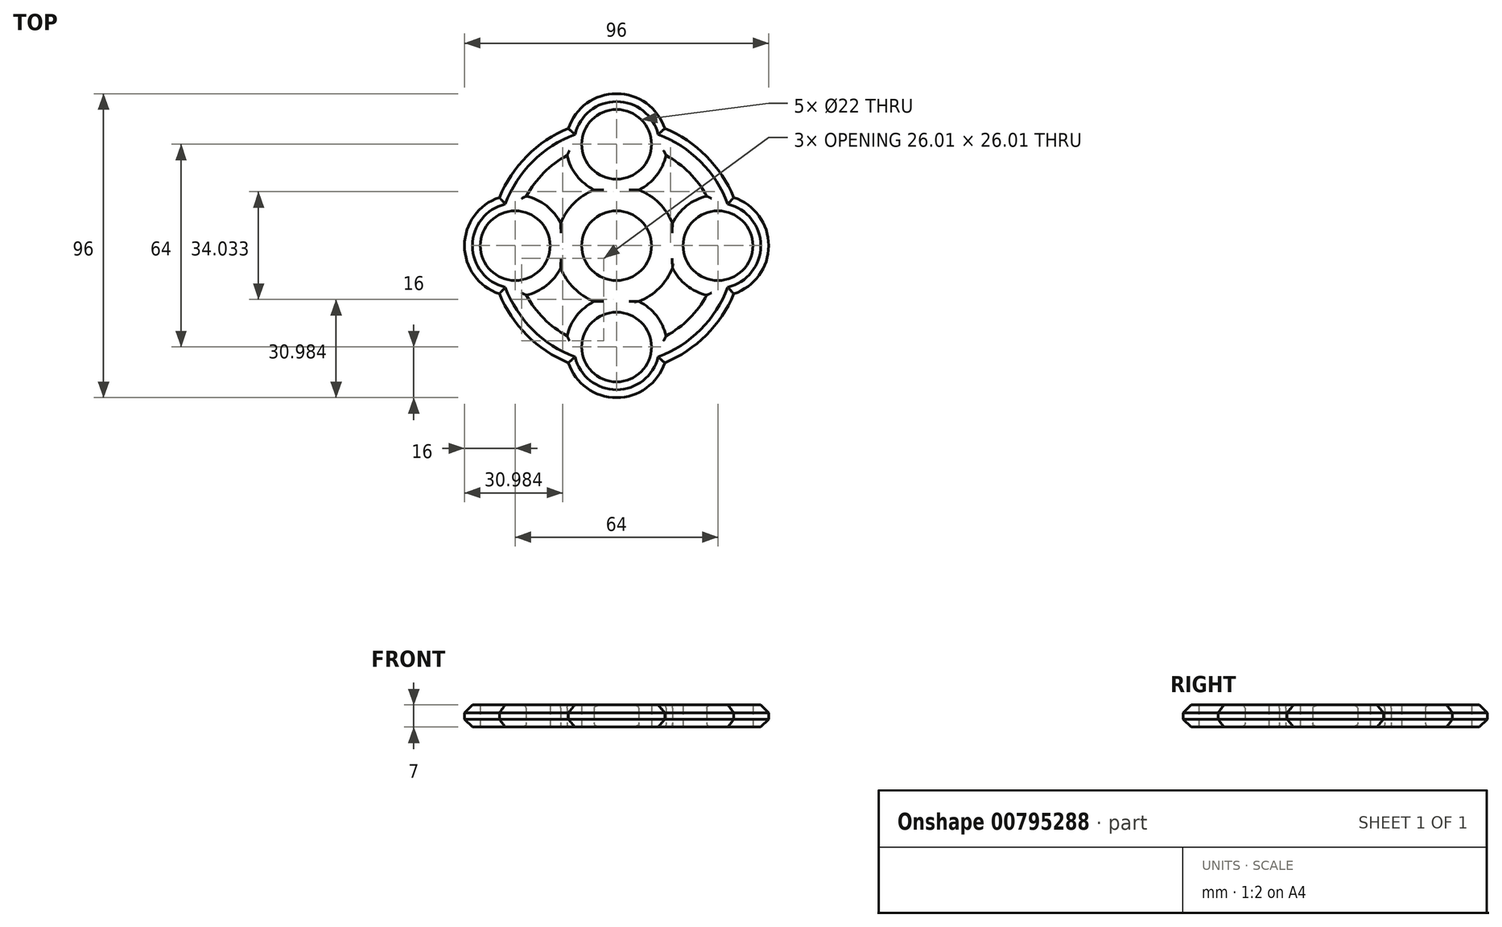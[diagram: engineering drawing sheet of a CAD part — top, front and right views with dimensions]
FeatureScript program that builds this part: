
annotation { "Feature Type Name" : "Feature", "Feature Type Description" : "" }
export const myFeature = defineFeature(function(context is Context, id is Id, definition is map)
    precondition{}
    {
        {
            var Q0;
            Q0=qCreatedBy(makeId("Top.planeOp"),FACE);
            var sketch = newSketch(context, id + "F0", { "sketchPlane" : qUnion([Q0])});
            skCircle(sketch, "E0", {"center": v(0, 0) * mm, "radius": 11 * mm});
            skCircle(sketch, "E1", {"center": v(0, 0) * mm, "radius": 19 * mm});
            skCircle(sketch, "E2", {"center": v(0, 0) * mm, "radius": 40 * mm});
            skCircle(sketch, "E3", {"center": v(0, 0) * mm, "radius": 32.5 * mm});
            skCircle(sketch, "E4", {"center": v(0, 32) * mm, "radius": 11 * mm});
            skCircle(sketch, "E5", {"center": v(0, 32) * mm, "radius": 16 * mm});
            skCircle(sketch, "E6.1.0", {"center": v(-32, 0) * mm, "radius": 16 * mm});
            skCircle(sketch, "E6.1.1", {"center": v(-32, 0) * mm, "radius": 11 * mm});
            skCircle(sketch, "E6.2.0", {"center": v(0, -32) * mm, "radius": 16 * mm});
            skCircle(sketch, "E6.2.1", {"center": v(0, -32) * mm, "radius": 11 * mm});
            skCircle(sketch, "E7.1.3.0", {"center": v(32, 0) * mm, "radius": 16 * mm});
            skCircle(sketch, "E7.2.3.0", {"center": v(32, 0) * mm, "radius": 11 * mm});
            skSolve(sketch);
        }
        {
            var Q0;
            {var subQ0=sQuery(id+"F0.wireOp",EDGE,"E6.1.0");var subQ1=sQuery(id+"F0.wireOp",EDGE,"E2");var subQ2=makeQuery(id+"F0.imprint","INTERSECT",VERTEX,{"disambiguationData":[OD(0.0)],"derivedFrom":[subQ1,subQ0]});Q0=makeQuery(id+"F0.imprint","IMPRINT",FACE,{"disambiguationData":[TD([[makeQuery(id+"F0.imprint","IMPRINT",EDGE,{"disambiguationData":[TD([[subQ2,-1.0]])],"derivedFrom":subQ1}),1.0]])]});}
            var Q1;
            {var subQ0=sQuery(id+"F0.wireOp",EDGE,"E6.1.0");var subQ1=sQuery(id+"F0.wireOp",EDGE,"E2");var subQ2=makeQuery(id+"F0.imprint","INTERSECT",VERTEX,{"disambiguationData":[OD(1.0)],"derivedFrom":[subQ1,subQ0]});Q1=makeQuery(id+"F0.imprint","IMPRINT",FACE,{"disambiguationData":[TD([[makeQuery(id+"F0.imprint","IMPRINT",EDGE,{"disambiguationData":[TD([[subQ2,1.0]])],"derivedFrom":subQ1}),1.0]])]});}
            var Q2;
            {var subQ0=sQuery(id+"F0.wireOp",EDGE,"E6.1.0");var subQ1=sQuery(id+"F0.wireOp",EDGE,"E2");var subQ2=makeQuery(id+"F0.imprint","INTERSECT",VERTEX,{"disambiguationData":[OD(1.0)],"derivedFrom":[subQ1,subQ0]});Q2=makeQuery(id+"F0.imprint","IMPRINT",FACE,{"disambiguationData":[TD([[makeQuery(id+"F0.imprint","IMPRINT",EDGE,{"disambiguationData":[TD([[subQ2,-1.0]])],"derivedFrom":subQ1}),1.0]])]});}
            var Q3;
            {var subQ0=sQuery(id+"F0.wireOp",EDGE,"E6.1.0");var subQ1=sQuery(id+"F0.wireOp",EDGE,"E2");var subQ2=makeQuery(id+"F0.imprint","INTERSECT",VERTEX,{"disambiguationData":[OD(0.0)],"derivedFrom":[subQ1,subQ0]});Q3=makeQuery(id+"F0.imprint","IMPRINT",FACE,{"disambiguationData":[TD([[makeQuery(id+"F0.imprint","IMPRINT",EDGE,{"disambiguationData":[TD([[subQ2,-1.0]])],"derivedFrom":subQ1}),-1.0]])]});}
            var Q4;
            {var subQ3=sQuery(id+"F0.wireOp",EDGE,"E6.1.0");var subQ5=sQuery(id+"F0.wireOp",EDGE,"E1");var subQ6=makeQuery(id+"F0.imprint","INTERSECT",VERTEX,{"disambiguationData":[OD(0.0)],"derivedFrom":[subQ5,subQ3]});Q4=makeQuery(id+"F0.imprint","IMPRINT",FACE,{"disambiguationData":[TD([[makeQuery(id+"F0.imprint","IMPRINT",EDGE,{"disambiguationData":[TD([[subQ6,-1.0]])],"derivedFrom":subQ5}),-1.0]])]});}
            var Q5;
            {var subQ0=sQuery(id+"F0.wireOp",EDGE,"E6.1.0");var subQ1=sQuery(id+"F0.wireOp",EDGE,"E1");var subQ2=makeQuery(id+"F0.imprint","INTERSECT",VERTEX,{"disambiguationData":[OD(0.0)],"derivedFrom":[subQ1,subQ0]});Q5=makeQuery(id+"F0.imprint","IMPRINT",FACE,{"disambiguationData":[TD([[makeQuery(id+"F0.imprint","IMPRINT",EDGE,{"disambiguationData":[TD([[subQ2,-1.0]])],"derivedFrom":subQ1}),1.0]])]});}
            var Q6;
            Q6=makeQuery(id+"F0.imprint","IMPRINT",FACE,{"disambiguationData":[TD([[makeQuery(id+"F0.imprint","IMPRINT",EDGE,{"derivedFrom":sQuery(id+"F0.wireOp",EDGE,"E0")}),-1.0]])]});
            var Q7;
            {var subQ0=sQuery(id+"F0.wireOp",EDGE,"E6.2.0");var subQ1=sQuery(id+"F0.wireOp",EDGE,"E1");var subQ2=makeQuery(id+"F0.imprint","INTERSECT",VERTEX,{"disambiguationData":[OD(0.0)],"derivedFrom":[subQ1,subQ0]});Q7=makeQuery(id+"F0.imprint","IMPRINT",FACE,{"disambiguationData":[TD([[makeQuery(id+"F0.imprint","IMPRINT",EDGE,{"disambiguationData":[TD([[subQ2,-1.0]])],"derivedFrom":subQ1}),1.0]])]});}
            var Q8;
            {var subQ0=sQuery(id+"F0.wireOp",EDGE,"E6.2.0");var subQ1=sQuery(id+"F0.wireOp",EDGE,"E1");var subQ9=makeQuery(id+"F0.imprint","INTERSECT",VERTEX,{"disambiguationData":[OD(0.0)],"derivedFrom":[subQ1,subQ0]});Q8=makeQuery(id+"F0.imprint","IMPRINT",FACE,{"disambiguationData":[TD([[makeQuery(id+"F0.imprint","IMPRINT",EDGE,{"disambiguationData":[TD([[subQ9,-1.0]])],"derivedFrom":subQ1}),-1.0]])]});}
            var Q9;
            {var subQ0=sQuery(id+"F0.wireOp",EDGE,"E6.2.0");var subQ1=sQuery(id+"F0.wireOp",EDGE,"E2");var subQ2=makeQuery(id+"F0.imprint","INTERSECT",VERTEX,{"disambiguationData":[OD(0.0)],"derivedFrom":[subQ1,subQ0]});Q9=makeQuery(id+"F0.imprint","IMPRINT",FACE,{"disambiguationData":[TD([[makeQuery(id+"F0.imprint","IMPRINT",EDGE,{"disambiguationData":[TD([[subQ2,-1.0]])],"derivedFrom":subQ1}),1.0]])]});}
            var Q10;
            {var subQ0=sQuery(id+"F0.wireOp",EDGE,"E6.2.0");var subQ1=sQuery(id+"F0.wireOp",EDGE,"E2");var subQ2=makeQuery(id+"F0.imprint","INTERSECT",VERTEX,{"disambiguationData":[OD(1.0)],"derivedFrom":[subQ1,subQ0]});Q10=makeQuery(id+"F0.imprint","IMPRINT",FACE,{"disambiguationData":[TD([[makeQuery(id+"F0.imprint","IMPRINT",EDGE,{"disambiguationData":[TD([[subQ2,1.0]])],"derivedFrom":subQ1}),1.0]])]});}
            var Q11;
            {var subQ0=sQuery(id+"F0.wireOp",EDGE,"E5");var subQ1=sQuery(id+"F0.wireOp",EDGE,"E2");var subQ2=makeQuery(id+"F0.imprint","INTERSECT",VERTEX,{"disambiguationData":[OD(0.0)],"derivedFrom":[subQ1,subQ0]});Q11=makeQuery(id+"F0.imprint","IMPRINT",FACE,{"disambiguationData":[TD([[makeQuery(id+"F0.imprint","IMPRINT",EDGE,{"disambiguationData":[TD([[subQ2,1.0]])],"derivedFrom":subQ1}),1.0]])]});}
            var Q12;
            {var subQ0=sQuery(id+"F0.wireOp",EDGE,"E6.2.0");var subQ1=sQuery(id+"F0.wireOp",EDGE,"E2");var subQ2=makeQuery(id+"F0.imprint","INTERSECT",VERTEX,{"disambiguationData":[OD(0.0)],"derivedFrom":[subQ1,subQ0]});Q12=makeQuery(id+"F0.imprint","IMPRINT",FACE,{"disambiguationData":[TD([[makeQuery(id+"F0.imprint","IMPRINT",EDGE,{"disambiguationData":[TD([[subQ2,-1.0]])],"derivedFrom":subQ1}),-1.0]])]});}
            var Q13;
            {var subQ0=sQuery(id+"F0.wireOp",EDGE,"E5");var subQ1=sQuery(id+"F0.wireOp",EDGE,"E1");var subQ2=makeQuery(id+"F0.imprint","INTERSECT",VERTEX,{"disambiguationData":[OD(0.0)],"derivedFrom":[subQ1,subQ0]});Q13=makeQuery(id+"F0.imprint","IMPRINT",FACE,{"disambiguationData":[TD([[makeQuery(id+"F0.imprint","IMPRINT",EDGE,{"disambiguationData":[TD([[subQ2,1.0]])],"derivedFrom":subQ1}),1.0]])]});}
            var Q14;
            {var subQ0=sQuery(id+"F0.wireOp",EDGE,"E5");var subQ1=sQuery(id+"F0.wireOp",EDGE,"E2");var subQ2=makeQuery(id+"F0.imprint","INTERSECT",VERTEX,{"disambiguationData":[OD(1.0)],"derivedFrom":[subQ1,subQ0]});Q14=makeQuery(id+"F0.imprint","IMPRINT",FACE,{"disambiguationData":[TD([[makeQuery(id+"F0.imprint","IMPRINT",EDGE,{"disambiguationData":[TD([[subQ2,-1.0]])],"derivedFrom":subQ1}),1.0]])]});}
            var Q15;
            {var subQ0=sQuery(id+"F0.wireOp",EDGE,"E5");var subQ1=sQuery(id+"F0.wireOp",EDGE,"E2");var subQ2=makeQuery(id+"F0.imprint","INTERSECT",VERTEX,{"disambiguationData":[OD(0.0)],"derivedFrom":[subQ1,subQ0]});Q15=makeQuery(id+"F0.imprint","IMPRINT",FACE,{"disambiguationData":[TD([[makeQuery(id+"F0.imprint","IMPRINT",EDGE,{"disambiguationData":[TD([[subQ2,-1.0]])],"derivedFrom":subQ1}),1.0]])]});}
            var Q16;
            {var subQ0=sQuery(id+"F0.wireOp",EDGE,"E5");var subQ1=sQuery(id+"F0.wireOp",EDGE,"E2");var subQ2=makeQuery(id+"F0.imprint","INTERSECT",VERTEX,{"disambiguationData":[OD(1.0)],"derivedFrom":[subQ1,subQ0]});Q16=makeQuery(id+"F0.imprint","IMPRINT",FACE,{"disambiguationData":[TD([[makeQuery(id+"F0.imprint","IMPRINT",EDGE,{"disambiguationData":[TD([[subQ2,1.0]])],"derivedFrom":subQ1}),1.0]])]});}
            var Q17;
            {var subQ0=sQuery(id+"F0.wireOp",EDGE,"E5");var subQ1=sQuery(id+"F0.wireOp",EDGE,"E2");var subQ2=makeQuery(id+"F0.imprint","INTERSECT",VERTEX,{"disambiguationData":[OD(0.0)],"derivedFrom":[subQ1,subQ0]});Q17=makeQuery(id+"F0.imprint","IMPRINT",FACE,{"disambiguationData":[TD([[makeQuery(id+"F0.imprint","IMPRINT",EDGE,{"disambiguationData":[TD([[subQ2,-1.0]])],"derivedFrom":subQ1}),-1.0]])]});}
            var Q18;
            {var subQ4=sQuery(id+"F0.wireOp",EDGE,"E5");var subQ7=sQuery(id+"F0.wireOp",EDGE,"E1");var subQ8=makeQuery(id+"F0.imprint","INTERSECT",VERTEX,{"disambiguationData":[OD(0.0)],"derivedFrom":[subQ7,subQ4]});Q18=makeQuery(id+"F0.imprint","IMPRINT",FACE,{"disambiguationData":[TD([[makeQuery(id+"F0.imprint","IMPRINT",EDGE,{"disambiguationData":[TD([[subQ8,-1.0]])],"derivedFrom":subQ7}),-1.0]])]});}
            var Q19;
            {var subQ0=sQuery(id+"F0.wireOp",EDGE,"E5");var subQ1=sQuery(id+"F0.wireOp",EDGE,"E1");var subQ2=makeQuery(id+"F0.imprint","INTERSECT",VERTEX,{"disambiguationData":[OD(0.0)],"derivedFrom":[subQ1,subQ0]});Q19=makeQuery(id+"F0.imprint","IMPRINT",FACE,{"disambiguationData":[TD([[makeQuery(id+"F0.imprint","IMPRINT",EDGE,{"disambiguationData":[TD([[subQ2,-1.0]])],"derivedFrom":subQ1}),1.0]])]});}
            var Q20;
            {var subQ0=sQuery(id+"F0.wireOp",EDGE,"E7.1.3.0");var subQ1=sQuery(id+"F0.wireOp",EDGE,"E1");var subQ2=makeQuery(id+"F0.imprint","INTERSECT",VERTEX,{"disambiguationData":[OD(0.0)],"derivedFrom":[subQ1,subQ0]});Q20=makeQuery(id+"F0.imprint","IMPRINT",FACE,{"disambiguationData":[TD([[makeQuery(id+"F0.imprint","IMPRINT",EDGE,{"disambiguationData":[TD([[subQ2,1.0]])],"derivedFrom":subQ1}),1.0]])]});}
            var Q21;
            {var subQ0=sQuery(id+"F0.wireOp",EDGE,"E7.1.3.0");var subQ7=sQuery(id+"F0.wireOp",EDGE,"E1");var subQ8=makeQuery(id+"F0.imprint","INTERSECT",VERTEX,{"disambiguationData":[OD(0.0)],"derivedFrom":[subQ7,subQ0]});Q21=makeQuery(id+"F0.imprint","IMPRINT",FACE,{"disambiguationData":[TD([[makeQuery(id+"F0.imprint","IMPRINT",EDGE,{"disambiguationData":[TD([[subQ8,1.0]])],"derivedFrom":subQ7}),-1.0]])]});}
            var Q22;
            {var subQ0=sQuery(id+"F0.wireOp",EDGE,"E7.1.3.0");var subQ1=sQuery(id+"F0.wireOp",EDGE,"E2");var subQ2=makeQuery(id+"F0.imprint","INTERSECT",VERTEX,{"disambiguationData":[OD(1.0)],"derivedFrom":[subQ1,subQ0]});Q22=makeQuery(id+"F0.imprint","IMPRINT",FACE,{"disambiguationData":[TD([[makeQuery(id+"F0.imprint","IMPRINT",EDGE,{"disambiguationData":[TD([[subQ2,-1.0]])],"derivedFrom":subQ1}),1.0]])]});}
            var Q23;
            {var subQ0=sQuery(id+"F0.wireOp",EDGE,"E7.1.3.0");var subQ1=sQuery(id+"F0.wireOp",EDGE,"E2");var subQ2=makeQuery(id+"F0.imprint","INTERSECT",VERTEX,{"disambiguationData":[OD(0.0)],"derivedFrom":[subQ1,subQ0]});Q23=makeQuery(id+"F0.imprint","IMPRINT",FACE,{"disambiguationData":[TD([[makeQuery(id+"F0.imprint","IMPRINT",EDGE,{"disambiguationData":[TD([[subQ2,1.0]])],"derivedFrom":subQ1}),1.0]])]});}
            var Q24;
            {var subQ0=sQuery(id+"F0.wireOp",EDGE,"E7.1.3.0");var subQ1=sQuery(id+"F0.wireOp",EDGE,"E2");var subQ2=makeQuery(id+"F0.imprint","INTERSECT",VERTEX,{"disambiguationData":[OD(0.0)],"derivedFrom":[subQ1,subQ0]});Q24=makeQuery(id+"F0.imprint","IMPRINT",FACE,{"disambiguationData":[TD([[makeQuery(id+"F0.imprint","IMPRINT",EDGE,{"disambiguationData":[TD([[subQ2,1.0]])],"derivedFrom":subQ1}),-1.0]])]});}
            var Q25;
            {var subQ0=sQuery(id+"F0.wireOp",EDGE,"E6.2.0");var subQ1=sQuery(id+"F0.wireOp",EDGE,"E2");var subQ2=makeQuery(id+"F0.imprint","INTERSECT",VERTEX,{"disambiguationData":[OD(1.0)],"derivedFrom":[subQ1,subQ0]});Q25=makeQuery(id+"F0.imprint","IMPRINT",FACE,{"disambiguationData":[TD([[makeQuery(id+"F0.imprint","IMPRINT",EDGE,{"disambiguationData":[TD([[subQ2,-1.0]])],"derivedFrom":subQ1}),1.0]])]});}
            extrude(context, id + "F1", {"entities" : qUnion([Q0, Q1, Q2, Q3, Q4, Q5, Q6, Q7, Q8, Q9, Q10, Q11, Q12, Q13, Q14, Q15, Q16, Q17, Q18, Q19, Q20, Q21, Q22, Q23, Q24, Q25]), "depth" : 7 * mm, "offsetDistance" : 25 * mm});
        }
        {
            var Q0;
            {var subQ0=sQuery(id+"F0.wireOp",EDGE,"E2");Q0=makeQuery(id+"F1.opExtrude","CAP_EDGE",EDGE,{"disambiguationData":[OSD([subQ0]),TDD([makeQuery(id+"F0.imprint","IMPRINT",EDGE,{"disambiguationData":[TD([[makeQuery(id+"F0.imprint","INTERSECT",VERTEX,{"disambiguationData":[OD(1.0)],"derivedFrom":[subQ0,sQuery(id+"F0.wireOp",EDGE,"E6.1.0")]}),-1.0]])],"derivedFrom":subQ0})])],"isStart":false});}
            var Q1;
            {var subQ0=sQuery(id+"F0.wireOp",EDGE,"E2");Q1=makeQuery(id+"F1.opExtrude","CAP_EDGE",EDGE,{"disambiguationData":[OSD([subQ0]),TDD([makeQuery(id+"F0.imprint","IMPRINT",EDGE,{"disambiguationData":[TD([[makeQuery(id+"F0.imprint","INTERSECT",VERTEX,{"disambiguationData":[OD(1.0)],"derivedFrom":[subQ0,sQuery(id+"F0.wireOp",EDGE,"E5")]}),-1.0]])],"derivedFrom":subQ0})])],"isStart":false});}
            var Q2;
            {var subQ0=sQuery(id+"F0.wireOp",EDGE,"E6.1.0");var subQ1=sQuery(id+"F0.wireOp",EDGE,"E2");Q2=makeQuery(id+"F1.opExtrude","CAP_EDGE",EDGE,{"disambiguationData":[OSD([subQ0]),TDD([makeQuery(id+"F0.imprint","IMPRINT",EDGE,{"disambiguationData":[TD([[makeQuery(id+"F0.imprint","INTERSECT",VERTEX,{"disambiguationData":[OD(0.0)],"derivedFrom":[subQ1,subQ0]}),-1.0]])],"derivedFrom":subQ0})])],"isStart":false});}
            var Q3;
            {var subQ0=sQuery(id+"F0.wireOp",EDGE,"E5");var subQ1=sQuery(id+"F0.wireOp",EDGE,"E2");Q3=makeQuery(id+"F1.opExtrude","CAP_EDGE",EDGE,{"disambiguationData":[OSD([subQ0]),TDD([makeQuery(id+"F0.imprint","IMPRINT",EDGE,{"disambiguationData":[TD([[makeQuery(id+"F0.imprint","INTERSECT",VERTEX,{"disambiguationData":[OD(0.0)],"derivedFrom":[subQ1,subQ0]}),-1.0]])],"derivedFrom":subQ0})])],"isStart":false});}
            var Q4;
            {var subQ0=sQuery(id+"F0.wireOp",EDGE,"E6.2.0");var subQ1=sQuery(id+"F0.wireOp",EDGE,"E2");Q4=makeQuery(id+"F1.opExtrude","CAP_EDGE",EDGE,{"disambiguationData":[OSD([subQ0]),TDD([makeQuery(id+"F0.imprint","IMPRINT",EDGE,{"disambiguationData":[TD([[makeQuery(id+"F0.imprint","INTERSECT",VERTEX,{"disambiguationData":[OD(0.0)],"derivedFrom":[subQ1,subQ0]}),-1.0]])],"derivedFrom":subQ0})])],"isStart":false});}
            var Q5;
            {var subQ0=sQuery(id+"F0.wireOp",EDGE,"E2");Q5=makeQuery(id+"F1.opExtrude","CAP_EDGE",EDGE,{"disambiguationData":[OSD([subQ0]),TDD([makeQuery(id+"F0.imprint","IMPRINT",EDGE,{"disambiguationData":[TD([[makeQuery(id+"F0.imprint","INTERSECT",VERTEX,{"disambiguationData":[OD(0.0)],"derivedFrom":[subQ0,sQuery(id+"F0.wireOp",EDGE,"E5")]}),1.0]])],"derivedFrom":subQ0})])],"isStart":false});}
            var Q6;
            {var subQ0=sQuery(id+"F0.wireOp",EDGE,"E2");Q6=makeQuery(id+"F1.opExtrude","CAP_EDGE",EDGE,{"disambiguationData":[OSD([subQ0]),TDD([makeQuery(id+"F0.imprint","IMPRINT",EDGE,{"disambiguationData":[TD([[makeQuery(id+"F0.imprint","INTERSECT",VERTEX,{"disambiguationData":[OD(0.0)],"derivedFrom":[subQ0,sQuery(id+"F0.wireOp",EDGE,"E5")]}),1.0]])],"derivedFrom":subQ0})])],"isStart":true});}
            var Q7;
            {var subQ0=sQuery(id+"F0.wireOp",EDGE,"E6.2.0");var subQ1=sQuery(id+"F0.wireOp",EDGE,"E2");Q7=makeQuery(id+"F1.opExtrude","CAP_EDGE",EDGE,{"disambiguationData":[OSD([subQ0]),TDD([makeQuery(id+"F0.imprint","IMPRINT",EDGE,{"disambiguationData":[TD([[makeQuery(id+"F0.imprint","INTERSECT",VERTEX,{"disambiguationData":[OD(0.0)],"derivedFrom":[subQ1,subQ0]}),-1.0]])],"derivedFrom":subQ0})])],"isStart":true});}
            var Q8;
            {var subQ0=sQuery(id+"F0.wireOp",EDGE,"E2");Q8=makeQuery(id+"F1.opExtrude","CAP_EDGE",EDGE,{"disambiguationData":[OSD([subQ0]),TDD([makeQuery(id+"F0.imprint","IMPRINT",EDGE,{"disambiguationData":[TD([[makeQuery(id+"F0.imprint","INTERSECT",VERTEX,{"disambiguationData":[OD(1.0)],"derivedFrom":[subQ0,sQuery(id+"F0.wireOp",EDGE,"E6.1.0")]}),-1.0]])],"derivedFrom":subQ0})])],"isStart":true});}
            var Q9;
            {var subQ0=sQuery(id+"F0.wireOp",EDGE,"E6.1.0");var subQ1=sQuery(id+"F0.wireOp",EDGE,"E2");Q9=makeQuery(id+"F1.opExtrude","CAP_EDGE",EDGE,{"disambiguationData":[OSD([subQ0]),TDD([makeQuery(id+"F0.imprint","IMPRINT",EDGE,{"disambiguationData":[TD([[makeQuery(id+"F0.imprint","INTERSECT",VERTEX,{"disambiguationData":[OD(0.0)],"derivedFrom":[subQ1,subQ0]}),-1.0]])],"derivedFrom":subQ0})])],"isStart":true});}
            var Q10;
            {var subQ0=sQuery(id+"F0.wireOp",EDGE,"E2");Q10=makeQuery(id+"F1.opExtrude","CAP_EDGE",EDGE,{"disambiguationData":[OSD([subQ0]),TDD([makeQuery(id+"F0.imprint","IMPRINT",EDGE,{"disambiguationData":[TD([[makeQuery(id+"F0.imprint","INTERSECT",VERTEX,{"disambiguationData":[OD(1.0)],"derivedFrom":[subQ0,sQuery(id+"F0.wireOp",EDGE,"E5")]}),-1.0]])],"derivedFrom":subQ0})])],"isStart":true});}
            var Q11;
            {var subQ0=sQuery(id+"F0.wireOp",EDGE,"E5");var subQ1=sQuery(id+"F0.wireOp",EDGE,"E2");Q11=makeQuery(id+"F1.opExtrude","CAP_EDGE",EDGE,{"disambiguationData":[OSD([subQ0]),TDD([makeQuery(id+"F0.imprint","IMPRINT",EDGE,{"disambiguationData":[TD([[makeQuery(id+"F0.imprint","INTERSECT",VERTEX,{"disambiguationData":[OD(0.0)],"derivedFrom":[subQ1,subQ0]}),-1.0]])],"derivedFrom":subQ0})])],"isStart":true});}
            var Q12;
            {var subQ0=sQuery(id+"F0.wireOp",EDGE,"E2");Q12=makeQuery(id+"F1.opExtrude","CAP_EDGE",EDGE,{"disambiguationData":[OSD([subQ0]),TDD([makeQuery(id+"F0.imprint","IMPRINT",EDGE,{"disambiguationData":[TD([[makeQuery(id+"F0.imprint","INTERSECT",VERTEX,{"disambiguationData":[OD(1.0)],"derivedFrom":[subQ0,sQuery(id+"F0.wireOp",EDGE,"E6.2.0")]}),-1.0]])],"derivedFrom":subQ0})])],"isStart":false});}
            var Q13;
            {var subQ0=sQuery(id+"F0.wireOp",EDGE,"E2");Q13=makeQuery(id+"F1.opExtrude","CAP_EDGE",EDGE,{"disambiguationData":[OSD([subQ0]),TDD([makeQuery(id+"F0.imprint","IMPRINT",EDGE,{"disambiguationData":[TD([[makeQuery(id+"F0.imprint","INTERSECT",VERTEX,{"disambiguationData":[OD(1.0)],"derivedFrom":[subQ0,sQuery(id+"F0.wireOp",EDGE,"E6.2.0")]}),-1.0]])],"derivedFrom":subQ0})])],"isStart":true});}
            var Q14;
            {var subQ0=sQuery(id+"F0.wireOp",EDGE,"E7.1.3.0");var subQ1=sQuery(id+"F0.wireOp",EDGE,"E2");Q14=makeQuery(id+"F1.opExtrude","CAP_EDGE",EDGE,{"disambiguationData":[OSD([subQ0]),TDD([makeQuery(id+"F0.imprint","IMPRINT",EDGE,{"disambiguationData":[TD([[makeQuery(id+"F0.imprint","INTERSECT",VERTEX,{"disambiguationData":[OD(0.0)],"derivedFrom":[subQ1,subQ0]}),1.0]])],"derivedFrom":subQ0})])],"isStart":false});}
            var Q15;
            {var subQ0=sQuery(id+"F0.wireOp",EDGE,"E7.1.3.0");var subQ1=sQuery(id+"F0.wireOp",EDGE,"E2");Q15=makeQuery(id+"F1.opExtrude","CAP_EDGE",EDGE,{"disambiguationData":[OSD([subQ0]),TDD([makeQuery(id+"F0.imprint","IMPRINT",EDGE,{"disambiguationData":[TD([[makeQuery(id+"F0.imprint","INTERSECT",VERTEX,{"disambiguationData":[OD(0.0)],"derivedFrom":[subQ1,subQ0]}),1.0]])],"derivedFrom":subQ0})])],"isStart":true});}
            chamfer(context, id + "F2", {"entities" : qUnion([Q0, Q1, Q2, Q3, Q4, Q5, Q6, Q7, Q8, Q9, Q10, Q11, Q12, Q13, Q14, Q15]), "width" : 2.5 * mm, "tangentPropagation" : true});
        }
        {
            var Q0;
            {var subQ0=sQuery(id+"F0.wireOp",EDGE,"E3");Q0=makeQuery(id+"F1.opExtrude","CAP_EDGE",EDGE,{"disambiguationData":[OSD([subQ0]),TDD([makeQuery(id+"F0.imprint","IMPRINT",EDGE,{"disambiguationData":[TD([[makeQuery(id+"F0.imprint","INTERSECT",VERTEX,{"disambiguationData":[OD(1.0)],"derivedFrom":[subQ0,sQuery(id+"F0.wireOp",EDGE,"E6.1.0")]}),-1.0]])],"derivedFrom":subQ0})])],"isStart":false});}
            var Q1;
            {var subQ0=sQuery(id+"F0.wireOp",EDGE,"E6.1.0");Q1=makeQuery(id+"F1.opExtrude","CAP_EDGE",EDGE,{"disambiguationData":[OSD([subQ0]),TDD([makeQuery(id+"F0.imprint","IMPRINT",EDGE,{"disambiguationData":[TD([[makeQuery(id+"F0.imprint","INTERSECT",VERTEX,{"disambiguationData":[OD(1.0)],"derivedFrom":[sQuery(id+"F0.wireOp",EDGE,"E1"),subQ0]}),1.0]])],"derivedFrom":subQ0})])],"isStart":false});}
            var Q2;
            {var subQ0=sQuery(id+"F0.wireOp",EDGE,"E1");Q2=makeQuery(id+"F1.opExtrude","CAP_EDGE",EDGE,{"disambiguationData":[OSD([subQ0]),TDD([makeQuery(id+"F0.imprint","IMPRINT",EDGE,{"disambiguationData":[TD([[makeQuery(id+"F0.imprint","INTERSECT",VERTEX,{"disambiguationData":[OD(1.0)],"derivedFrom":[subQ0,sQuery(id+"F0.wireOp",EDGE,"E6.1.0")]}),-1.0]])],"derivedFrom":subQ0})])],"isStart":false});}
            var Q3;
            {var subQ0=sQuery(id+"F0.wireOp",EDGE,"E6.2.0");Q3=makeQuery(id+"F1.opExtrude","CAP_EDGE",EDGE,{"disambiguationData":[OSD([subQ0]),TDD([makeQuery(id+"F0.imprint","IMPRINT",EDGE,{"disambiguationData":[TD([[makeQuery(id+"F0.imprint","INTERSECT",VERTEX,{"disambiguationData":[OD(0.0)],"derivedFrom":[sQuery(id+"F0.wireOp",EDGE,"E1"),subQ0]}),-1.0]])],"derivedFrom":subQ0})])],"isStart":false});}
            var Q4;
            {var subQ0=sQuery(id+"F0.wireOp",EDGE,"E1");Q4=makeQuery(id+"F1.opExtrude","CAP_EDGE",EDGE,{"disambiguationData":[OSD([subQ0]),TDD([makeQuery(id+"F0.imprint","IMPRINT",EDGE,{"disambiguationData":[TD([[makeQuery(id+"F0.imprint","INTERSECT",VERTEX,{"disambiguationData":[OD(1.0)],"derivedFrom":[subQ0,sQuery(id+"F0.wireOp",EDGE,"E5")]}),1.0]])],"derivedFrom":subQ0})])],"isStart":false});}
            var Q5;
            {var subQ0=sQuery(id+"F0.wireOp",EDGE,"E5");Q5=makeQuery(id+"F1.opExtrude","CAP_EDGE",EDGE,{"disambiguationData":[OSD([subQ0]),TDD([makeQuery(id+"F0.imprint","IMPRINT",EDGE,{"disambiguationData":[TD([[makeQuery(id+"F0.imprint","INTERSECT",VERTEX,{"disambiguationData":[OD(1.0)],"derivedFrom":[sQuery(id+"F0.wireOp",EDGE,"E1"),subQ0]}),-1.0]])],"derivedFrom":subQ0})])],"isStart":false});}
            var Q6;
            {var subQ0=sQuery(id+"F0.wireOp",EDGE,"E3");Q6=makeQuery(id+"F1.opExtrude","CAP_EDGE",EDGE,{"disambiguationData":[OSD([subQ0]),TDD([makeQuery(id+"F0.imprint","IMPRINT",EDGE,{"disambiguationData":[TD([[makeQuery(id+"F0.imprint","INTERSECT",VERTEX,{"disambiguationData":[OD(0.0)],"derivedFrom":[subQ0,sQuery(id+"F0.wireOp",EDGE,"E5")]}),1.0]])],"derivedFrom":subQ0})])],"isStart":false});}
            var Q7;
            {var subQ0=sQuery(id+"F0.wireOp",EDGE,"E6.2.0");Q7=makeQuery(id+"F1.opExtrude","CAP_EDGE",EDGE,{"disambiguationData":[OSD([subQ0]),TDD([makeQuery(id+"F0.imprint","IMPRINT",EDGE,{"disambiguationData":[TD([[makeQuery(id+"F0.imprint","INTERSECT",VERTEX,{"disambiguationData":[OD(1.0)],"derivedFrom":[sQuery(id+"F0.wireOp",EDGE,"E1"),subQ0]}),1.0]])],"derivedFrom":subQ0})])],"isStart":false});}
            var Q8;
            {var subQ0=sQuery(id+"F0.wireOp",EDGE,"E6.1.0");Q8=makeQuery(id+"F1.opExtrude","CAP_EDGE",EDGE,{"disambiguationData":[OSD([subQ0]),TDD([makeQuery(id+"F0.imprint","IMPRINT",EDGE,{"disambiguationData":[TD([[makeQuery(id+"F0.imprint","INTERSECT",VERTEX,{"disambiguationData":[OD(0.0)],"derivedFrom":[sQuery(id+"F0.wireOp",EDGE,"E1"),subQ0]}),-1.0]])],"derivedFrom":subQ0})])],"isStart":false});}
            var Q9;
            {var subQ0=sQuery(id+"F0.wireOp",EDGE,"E1");Q9=makeQuery(id+"F1.opExtrude","CAP_EDGE",EDGE,{"disambiguationData":[OSD([subQ0]),TDD([makeQuery(id+"F0.imprint","IMPRINT",EDGE,{"disambiguationData":[TD([[makeQuery(id+"F0.imprint","INTERSECT",VERTEX,{"disambiguationData":[OD(0.0)],"derivedFrom":[subQ0,sQuery(id+"F0.wireOp",EDGE,"E5")]}),-1.0]])],"derivedFrom":subQ0})])],"isStart":false});}
            var Q10;
            {var subQ0=sQuery(id+"F0.wireOp",EDGE,"E5");Q10=makeQuery(id+"F1.opExtrude","CAP_EDGE",EDGE,{"disambiguationData":[OSD([subQ0]),TDD([makeQuery(id+"F0.imprint","IMPRINT",EDGE,{"disambiguationData":[TD([[makeQuery(id+"F0.imprint","INTERSECT",VERTEX,{"disambiguationData":[OD(0.0)],"derivedFrom":[sQuery(id+"F0.wireOp",EDGE,"E1"),subQ0]}),1.0]])],"derivedFrom":subQ0})])],"isStart":false});}
            var Q11;
            {var subQ0=sQuery(id+"F0.wireOp",EDGE,"E3");Q11=makeQuery(id+"F1.opExtrude","CAP_EDGE",EDGE,{"disambiguationData":[OSD([subQ0]),TDD([makeQuery(id+"F0.imprint","IMPRINT",EDGE,{"disambiguationData":[TD([[makeQuery(id+"F0.imprint","INTERSECT",VERTEX,{"disambiguationData":[OD(1.0)],"derivedFrom":[subQ0,sQuery(id+"F0.wireOp",EDGE,"E5")]}),-1.0]])],"derivedFrom":subQ0})])],"isStart":false});}
            var Q12;
            {var subQ0=sQuery(id+"F0.wireOp",EDGE,"E3");Q12=makeQuery(id+"F1.opExtrude","CAP_EDGE",EDGE,{"disambiguationData":[OSD([subQ0]),TDD([makeQuery(id+"F0.imprint","IMPRINT",EDGE,{"disambiguationData":[TD([[makeQuery(id+"F0.imprint","INTERSECT",VERTEX,{"disambiguationData":[OD(1.0)],"derivedFrom":[subQ0,sQuery(id+"F0.wireOp",EDGE,"E5")]}),-1.0]])],"derivedFrom":subQ0})])],"isStart":true});}
            var Q13;
            {var subQ0=sQuery(id+"F0.wireOp",EDGE,"E5");Q13=makeQuery(id+"F1.opExtrude","CAP_EDGE",EDGE,{"disambiguationData":[OSD([subQ0]),TDD([makeQuery(id+"F0.imprint","IMPRINT",EDGE,{"disambiguationData":[TD([[makeQuery(id+"F0.imprint","INTERSECT",VERTEX,{"disambiguationData":[OD(0.0)],"derivedFrom":[sQuery(id+"F0.wireOp",EDGE,"E1"),subQ0]}),1.0]])],"derivedFrom":subQ0})])],"isStart":true});}
            var Q14;
            {var subQ0=sQuery(id+"F0.wireOp",EDGE,"E1");Q14=makeQuery(id+"F1.opExtrude","CAP_EDGE",EDGE,{"disambiguationData":[OSD([subQ0]),TDD([makeQuery(id+"F0.imprint","IMPRINT",EDGE,{"disambiguationData":[TD([[makeQuery(id+"F0.imprint","INTERSECT",VERTEX,{"disambiguationData":[OD(0.0)],"derivedFrom":[subQ0,sQuery(id+"F0.wireOp",EDGE,"E5")]}),-1.0]])],"derivedFrom":subQ0})])],"isStart":true});}
            var Q15;
            {var subQ0=sQuery(id+"F0.wireOp",EDGE,"E6.1.0");Q15=makeQuery(id+"F1.opExtrude","CAP_EDGE",EDGE,{"disambiguationData":[OSD([subQ0]),TDD([makeQuery(id+"F0.imprint","IMPRINT",EDGE,{"disambiguationData":[TD([[makeQuery(id+"F0.imprint","INTERSECT",VERTEX,{"disambiguationData":[OD(0.0)],"derivedFrom":[sQuery(id+"F0.wireOp",EDGE,"E1"),subQ0]}),-1.0]])],"derivedFrom":subQ0})])],"isStart":true});}
            var Q16;
            {var subQ0=sQuery(id+"F0.wireOp",EDGE,"E3");Q16=makeQuery(id+"F1.opExtrude","CAP_EDGE",EDGE,{"disambiguationData":[OSD([subQ0]),TDD([makeQuery(id+"F0.imprint","IMPRINT",EDGE,{"disambiguationData":[TD([[makeQuery(id+"F0.imprint","INTERSECT",VERTEX,{"disambiguationData":[OD(1.0)],"derivedFrom":[subQ0,sQuery(id+"F0.wireOp",EDGE,"E6.1.0")]}),-1.0]])],"derivedFrom":subQ0})])],"isStart":true});}
            var Q17;
            {var subQ0=sQuery(id+"F0.wireOp",EDGE,"E6.1.0");Q17=makeQuery(id+"F1.opExtrude","CAP_EDGE",EDGE,{"disambiguationData":[OSD([subQ0]),TDD([makeQuery(id+"F0.imprint","IMPRINT",EDGE,{"disambiguationData":[TD([[makeQuery(id+"F0.imprint","INTERSECT",VERTEX,{"disambiguationData":[OD(1.0)],"derivedFrom":[sQuery(id+"F0.wireOp",EDGE,"E1"),subQ0]}),1.0]])],"derivedFrom":subQ0})])],"isStart":true});}
            var Q18;
            {var subQ0=sQuery(id+"F0.wireOp",EDGE,"E6.2.0");Q18=makeQuery(id+"F1.opExtrude","CAP_EDGE",EDGE,{"disambiguationData":[OSD([subQ0]),TDD([makeQuery(id+"F0.imprint","IMPRINT",EDGE,{"disambiguationData":[TD([[makeQuery(id+"F0.imprint","INTERSECT",VERTEX,{"disambiguationData":[OD(0.0)],"derivedFrom":[sQuery(id+"F0.wireOp",EDGE,"E1"),subQ0]}),-1.0]])],"derivedFrom":subQ0})])],"isStart":true});}
            var Q19;
            {var subQ0=sQuery(id+"F0.wireOp",EDGE,"E1");Q19=makeQuery(id+"F1.opExtrude","CAP_EDGE",EDGE,{"disambiguationData":[OSD([subQ0]),TDD([makeQuery(id+"F0.imprint","IMPRINT",EDGE,{"disambiguationData":[TD([[makeQuery(id+"F0.imprint","INTERSECT",VERTEX,{"disambiguationData":[OD(1.0)],"derivedFrom":[subQ0,sQuery(id+"F0.wireOp",EDGE,"E6.1.0")]}),-1.0]])],"derivedFrom":subQ0})])],"isStart":true});}
            var Q20;
            {var subQ0=sQuery(id+"F0.wireOp",EDGE,"E1");Q20=makeQuery(id+"F1.opExtrude","CAP_EDGE",EDGE,{"disambiguationData":[OSD([subQ0]),TDD([makeQuery(id+"F0.imprint","IMPRINT",EDGE,{"disambiguationData":[TD([[makeQuery(id+"F0.imprint","INTERSECT",VERTEX,{"disambiguationData":[OD(1.0)],"derivedFrom":[subQ0,sQuery(id+"F0.wireOp",EDGE,"E5")]}),1.0]])],"derivedFrom":subQ0})])],"isStart":true});}
            var Q21;
            {var subQ0=sQuery(id+"F0.wireOp",EDGE,"E5");Q21=makeQuery(id+"F1.opExtrude","CAP_EDGE",EDGE,{"disambiguationData":[OSD([subQ0]),TDD([makeQuery(id+"F0.imprint","IMPRINT",EDGE,{"disambiguationData":[TD([[makeQuery(id+"F0.imprint","INTERSECT",VERTEX,{"disambiguationData":[OD(1.0)],"derivedFrom":[sQuery(id+"F0.wireOp",EDGE,"E1"),subQ0]}),-1.0]])],"derivedFrom":subQ0})])],"isStart":true});}
            var Q22;
            {var subQ0=sQuery(id+"F0.wireOp",EDGE,"E3");Q22=makeQuery(id+"F1.opExtrude","CAP_EDGE",EDGE,{"disambiguationData":[OSD([subQ0]),TDD([makeQuery(id+"F0.imprint","IMPRINT",EDGE,{"disambiguationData":[TD([[makeQuery(id+"F0.imprint","INTERSECT",VERTEX,{"disambiguationData":[OD(0.0)],"derivedFrom":[subQ0,sQuery(id+"F0.wireOp",EDGE,"E5")]}),1.0]])],"derivedFrom":subQ0})])],"isStart":true});}
            var Q23;
            {var subQ0=sQuery(id+"F0.wireOp",EDGE,"E6.2.0");Q23=makeQuery(id+"F1.opExtrude","CAP_EDGE",EDGE,{"disambiguationData":[OSD([subQ0]),TDD([makeQuery(id+"F0.imprint","IMPRINT",EDGE,{"disambiguationData":[TD([[makeQuery(id+"F0.imprint","INTERSECT",VERTEX,{"disambiguationData":[OD(1.0)],"derivedFrom":[sQuery(id+"F0.wireOp",EDGE,"E1"),subQ0]}),1.0]])],"derivedFrom":subQ0})])],"isStart":true});}
            var Q24;
            {var subQ0=sQuery(id+"F0.wireOp",EDGE,"E1");Q24=makeQuery(id+"F1.opExtrude","CAP_EDGE",EDGE,{"disambiguationData":[OSD([subQ0]),TDD([makeQuery(id+"F0.imprint","IMPRINT",EDGE,{"disambiguationData":[TD([[makeQuery(id+"F0.imprint","INTERSECT",VERTEX,{"disambiguationData":[OD(0.0)],"derivedFrom":[subQ0,sQuery(id+"F0.wireOp",EDGE,"E5")]}),1.0]])],"derivedFrom":subQ0})])],"isStart":false});}
            var Q25;
            {var subQ0=sQuery(id+"F0.wireOp",EDGE,"E1");Q25=makeQuery(id+"F1.opExtrude","CAP_EDGE",EDGE,{"disambiguationData":[OSD([subQ0]),TDD([makeQuery(id+"F0.imprint","IMPRINT",EDGE,{"disambiguationData":[TD([[makeQuery(id+"F0.imprint","INTERSECT",VERTEX,{"disambiguationData":[OD(0.0)],"derivedFrom":[subQ0,sQuery(id+"F0.wireOp",EDGE,"E5")]}),1.0]])],"derivedFrom":subQ0})])],"isStart":true});}
            var Q26;
            {var subQ0=sQuery(id+"F0.wireOp",EDGE,"E5");Q26=makeQuery(id+"F1.opExtrude","CAP_EDGE",EDGE,{"disambiguationData":[OSD([subQ0]),TDD([makeQuery(id+"F0.imprint","IMPRINT",EDGE,{"disambiguationData":[TD([[makeQuery(id+"F0.imprint","INTERSECT",VERTEX,{"disambiguationData":[OD(0.0)],"derivedFrom":[sQuery(id+"F0.wireOp",EDGE,"E1"),subQ0]}),-1.0]])],"derivedFrom":subQ0})])],"isStart":false});}
            var Q27;
            {var subQ0=sQuery(id+"F0.wireOp",EDGE,"E7.1.3.0");Q27=makeQuery(id+"F1.opExtrude","CAP_EDGE",EDGE,{"disambiguationData":[OSD([subQ0]),TDD([makeQuery(id+"F0.imprint","IMPRINT",EDGE,{"disambiguationData":[TD([[makeQuery(id+"F0.imprint","INTERSECT",VERTEX,{"disambiguationData":[OD(0.0)],"derivedFrom":[sQuery(id+"F0.wireOp",EDGE,"E1"),subQ0]}),1.0]])],"derivedFrom":subQ0})])],"isStart":false});}
            var Q28;
            {var subQ0=sQuery(id+"F0.wireOp",EDGE,"E5");Q28=makeQuery(id+"F1.opExtrude","CAP_EDGE",EDGE,{"disambiguationData":[OSD([subQ0]),TDD([makeQuery(id+"F0.imprint","IMPRINT",EDGE,{"disambiguationData":[TD([[makeQuery(id+"F0.imprint","INTERSECT",VERTEX,{"disambiguationData":[OD(0.0)],"derivedFrom":[sQuery(id+"F0.wireOp",EDGE,"E1"),subQ0]}),-1.0]])],"derivedFrom":subQ0})])],"isStart":true});}
            var Q29;
            {var subQ0=sQuery(id+"F0.wireOp",EDGE,"E7.1.3.0");Q29=makeQuery(id+"F1.opExtrude","CAP_EDGE",EDGE,{"disambiguationData":[OSD([subQ0]),TDD([makeQuery(id+"F0.imprint","IMPRINT",EDGE,{"disambiguationData":[TD([[makeQuery(id+"F0.imprint","INTERSECT",VERTEX,{"disambiguationData":[OD(0.0)],"derivedFrom":[sQuery(id+"F0.wireOp",EDGE,"E1"),subQ0]}),1.0]])],"derivedFrom":subQ0})])],"isStart":true});}
            var Q30;
            {var subQ0=sQuery(id+"F0.wireOp",EDGE,"E1");Q30=makeQuery(id+"F1.opExtrude","CAP_EDGE",EDGE,{"disambiguationData":[OSD([subQ0]),TDD([makeQuery(id+"F0.imprint","IMPRINT",EDGE,{"disambiguationData":[TD([[makeQuery(id+"F0.imprint","INTERSECT",VERTEX,{"disambiguationData":[OD(1.0)],"derivedFrom":[subQ0,sQuery(id+"F0.wireOp",EDGE,"E6.2.0")]}),-1.0]])],"derivedFrom":subQ0})])],"isStart":false});}
            var Q31;
            {var subQ0=sQuery(id+"F0.wireOp",EDGE,"E7.1.3.0");Q31=makeQuery(id+"F1.opExtrude","CAP_EDGE",EDGE,{"disambiguationData":[OSD([subQ0]),TDD([makeQuery(id+"F0.imprint","IMPRINT",EDGE,{"disambiguationData":[TD([[makeQuery(id+"F0.imprint","INTERSECT",VERTEX,{"disambiguationData":[OD(1.0)],"derivedFrom":[sQuery(id+"F0.wireOp",EDGE,"E1"),subQ0]}),-1.0]])],"derivedFrom":subQ0})])],"isStart":false});}
            var Q32;
            {var subQ0=sQuery(id+"F0.wireOp",EDGE,"E3");Q32=makeQuery(id+"F1.opExtrude","CAP_EDGE",EDGE,{"disambiguationData":[OSD([subQ0]),TDD([makeQuery(id+"F0.imprint","IMPRINT",EDGE,{"disambiguationData":[TD([[makeQuery(id+"F0.imprint","INTERSECT",VERTEX,{"disambiguationData":[OD(1.0)],"derivedFrom":[subQ0,sQuery(id+"F0.wireOp",EDGE,"E6.2.0")]}),-1.0]])],"derivedFrom":subQ0})])],"isStart":false});}
            var Q33;
            {var subQ0=sQuery(id+"F0.wireOp",EDGE,"E1");Q33=makeQuery(id+"F1.opExtrude","CAP_EDGE",EDGE,{"disambiguationData":[OSD([subQ0]),TDD([makeQuery(id+"F0.imprint","IMPRINT",EDGE,{"disambiguationData":[TD([[makeQuery(id+"F0.imprint","INTERSECT",VERTEX,{"disambiguationData":[OD(1.0)],"derivedFrom":[subQ0,sQuery(id+"F0.wireOp",EDGE,"E5")]}),-1.0]])],"derivedFrom":subQ0})])],"isStart":false});}
            var Q34;
            {var subQ0=sQuery(id+"F0.wireOp",EDGE,"E5");Q34=makeQuery(id+"F1.opExtrude","CAP_EDGE",EDGE,{"disambiguationData":[OSD([subQ0]),TDD([makeQuery(id+"F0.imprint","IMPRINT",EDGE,{"disambiguationData":[TD([[makeQuery(id+"F0.imprint","INTERSECT",VERTEX,{"disambiguationData":[OD(1.0)],"derivedFrom":[sQuery(id+"F0.wireOp",EDGE,"E1"),subQ0]}),1.0]])],"derivedFrom":subQ0})])],"isStart":false});}
            var Q35;
            {var subQ0=sQuery(id+"F0.wireOp",EDGE,"E1");Q35=makeQuery(id+"F1.opExtrude","CAP_EDGE",EDGE,{"disambiguationData":[OSD([subQ0]),TDD([makeQuery(id+"F0.imprint","IMPRINT",EDGE,{"disambiguationData":[TD([[makeQuery(id+"F0.imprint","INTERSECT",VERTEX,{"disambiguationData":[OD(1.0)],"derivedFrom":[subQ0,sQuery(id+"F0.wireOp",EDGE,"E5")]}),-1.0]])],"derivedFrom":subQ0})])],"isStart":true});}
            var Q36;
            {var subQ0=sQuery(id+"F0.wireOp",EDGE,"E5");Q36=makeQuery(id+"F1.opExtrude","CAP_EDGE",EDGE,{"disambiguationData":[OSD([subQ0]),TDD([makeQuery(id+"F0.imprint","IMPRINT",EDGE,{"disambiguationData":[TD([[makeQuery(id+"F0.imprint","INTERSECT",VERTEX,{"disambiguationData":[OD(1.0)],"derivedFrom":[sQuery(id+"F0.wireOp",EDGE,"E1"),subQ0]}),1.0]])],"derivedFrom":subQ0})])],"isStart":true});}
            var Q37;
            {var subQ0=sQuery(id+"F0.wireOp",EDGE,"E3");Q37=makeQuery(id+"F1.opExtrude","CAP_EDGE",EDGE,{"disambiguationData":[OSD([subQ0]),TDD([makeQuery(id+"F0.imprint","IMPRINT",EDGE,{"disambiguationData":[TD([[makeQuery(id+"F0.imprint","INTERSECT",VERTEX,{"disambiguationData":[OD(1.0)],"derivedFrom":[subQ0,sQuery(id+"F0.wireOp",EDGE,"E6.2.0")]}),-1.0]])],"derivedFrom":subQ0})])],"isStart":true});}
            var Q38;
            {var subQ0=sQuery(id+"F0.wireOp",EDGE,"E7.1.3.0");Q38=makeQuery(id+"F1.opExtrude","CAP_EDGE",EDGE,{"disambiguationData":[OSD([subQ0]),TDD([makeQuery(id+"F0.imprint","IMPRINT",EDGE,{"disambiguationData":[TD([[makeQuery(id+"F0.imprint","INTERSECT",VERTEX,{"disambiguationData":[OD(1.0)],"derivedFrom":[sQuery(id+"F0.wireOp",EDGE,"E1"),subQ0]}),-1.0]])],"derivedFrom":subQ0})])],"isStart":true});}
            fillet(context, id + "F3", {"entities" : qUnion([Q0, Q1, Q2, Q3, Q4, Q5, Q6, Q7, Q8, Q9, Q10, Q11, Q12, Q13, Q14, Q15, Q16, Q17, Q18, Q19, Q20, Q21, Q22, Q23, Q24, Q25, Q26, Q27, Q28, Q29, Q30, Q31, Q32, Q33, Q34, Q35, Q36, Q37, Q38]), "radius" : 1 * mm, "tangentPropagation" : true, "allowEdgeOverflow" : false});
        }
    });
